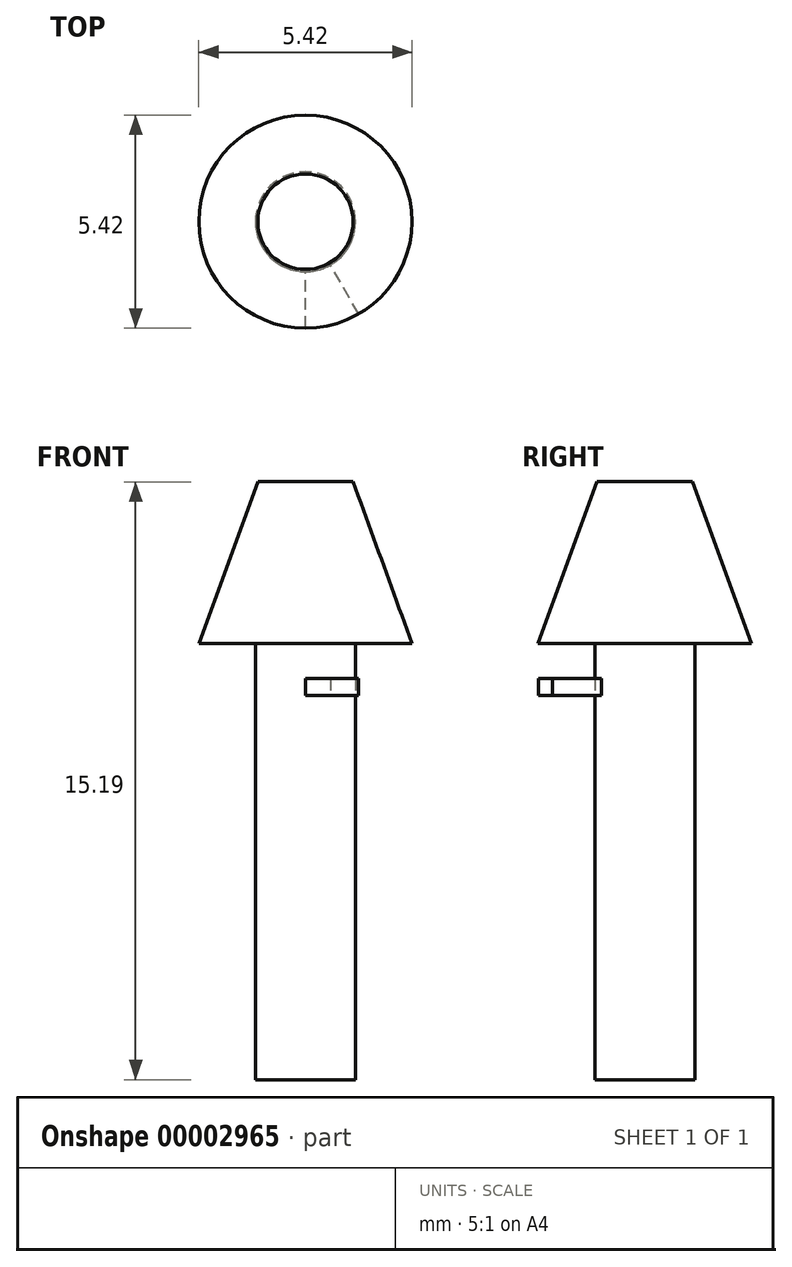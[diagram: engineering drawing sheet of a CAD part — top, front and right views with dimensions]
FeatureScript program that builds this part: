
annotation { "Feature Type Name" : "Feature", "Feature Type Description" : "" }
export const myFeature = defineFeature(function(context is Context, id is Id, definition is map)
    precondition{}
    {
        {
            var Q0;
            Q0=qCreatedBy(makeId("Top.planeOp"),FACE);
            var sketch = newSketch(context, id + "F0", { "sketchPlane" : qUnion([Q0])});
            skCircle(sketch, "E0", {"center": v(0, 0) * mm, "radius": 1.27 * mm});
            skSolve(sketch);
        }
        {
            var Q0;
            Q0=makeQuery(id+"F0.imprint","IMPRINT",FACE,{"disambiguationData":[TD([[makeQuery(id+"F0.imprint","IMPRINT",EDGE,{"derivedFrom":sQuery(id+"F0.wireOp",EDGE,"E0")}),1.0]])]});
            extrude(context, id + "F1", {"entities" : qUnion([Q0]), "depth" : 12.7 * mm});
        }
        {
            var Q0;
            Q0=qCreatedBy(makeId("Right.planeOp"),FACE);
            var sketch = newSketch(context, id + "F2", { "sketchPlane" : qUnion([Q0])});
            skLineSegment(sketch, "E1", {"start": v(-2.7, 11.08) * mm, "end": v(0, 11.08) * mm});
            skLineSegment(sketch, "E2", {"start": v(0, 11.08) * mm, "end": v(0, 15.2) * mm});
            skLineSegment(sketch, "E3", {"start": v(0, 15.2) * mm, "end": v(-1.21, 15.2) * mm});
            skLineSegment(sketch, "E4", {"start": v(-1.21, 15.2) * mm, "end": v(-2.7, 11.08) * mm});
            skLineSegment(sketch, "E5.bottom", {"start": v(-2.7, 9.76) * mm, "end": v(-1.05, 9.76) * mm});
            skLineSegment(sketch, "E5.top", {"start": v(-2.7, 10.19) * mm, "end": v(-1.05, 10.19) * mm});
            skLineSegment(sketch, "E5.left", {"start": v(-2.7, 9.76) * mm, "end": v(-2.7, 10.19) * mm});
            skLineSegment(sketch, "E5.right", {"start": v(-1.05, 9.76) * mm, "end": v(-1.05, 10.19) * mm});
            skSolve(sketch);
        }
        {
            var Q0;
            Q0=makeQuery(id+"F2.imprint","IMPRINT",FACE,{"disambiguationData":[TD([[makeQuery(id+"F2.imprint","IMPRINT",EDGE,{"derivedFrom":sQuery(id+"F2.wireOp",EDGE,"E1")}),1.0]])]});
            var Q1;
            Q1=makeQuery(id+"F1.opExtrude","CAP_EDGE",EDGE,{"disambiguationData":[OSD([sQuery(id+"F0.wireOp",EDGE,"E0")])],"isStart":false});
            revolve(context, id + "F3", {"operationType" : NewBodyOperationType.ADD, "entities" : qUnion([Q0]), "axis" : qUnion([Q1]), "revolveType" : RevolveType.FULL, "oppositeDirection" : true});
        }
        {
            var Q0;
            Q0=makeQuery(id+"F2.imprint","IMPRINT",FACE,{"disambiguationData":[TD([[makeQuery(id+"F2.imprint","IMPRINT",EDGE,{"derivedFrom":sQuery(id+"F2.wireOp",EDGE,"E5.bottom")}),1.0]])]});
            var Q1;
            Q1=makeQuery(id+"F3.opRevolve","SWEPT_EDGE",EDGE,{"disambiguationData":[OSD([sQuery(id+"F2.wireOp",EDGE,"E3"),sQuery(id+"F2.wireOp",EDGE,"E4")])]});
            revolve(context, id + "F4", {"operationType" : NewBodyOperationType.ADD, "entities" : qUnion([Q0]), "axis" : qUnion([Q1]), "revolveType" : RevolveType.ONE_DIRECTION, "angle" : 30 * degree});
        }
    });
